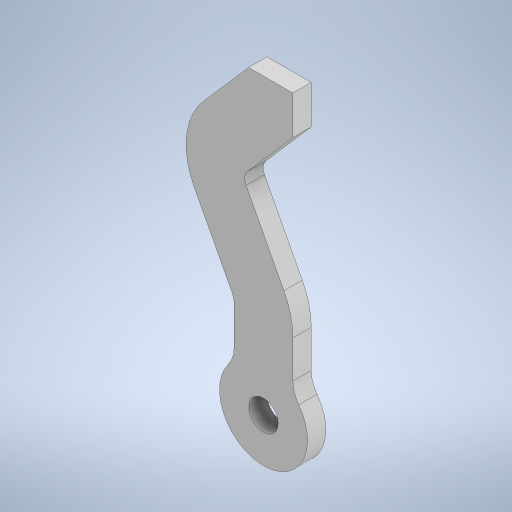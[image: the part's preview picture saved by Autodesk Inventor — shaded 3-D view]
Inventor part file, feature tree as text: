
AUTODESK INVENTOR PART (.ipt)
format: ipt  version: 2023.2 (Build 272271000, 271)  size: 268,288 bytes
history: native  units: mm
features: other x3, sketch x2, extrude x1
ambient origin geometry x8: Origin, YZ Plane, XZ Plane, XY Plane, X Axis, Y Axis, Z Axis, Center Point
bodies: Solid1 (feature_tree)
feature tree (6):
  other  "gripper.ipt"
  extrude  "Extrusion1"  Depth=4.0mm
  other  "Solid1::gripper.ipt"
  other  "TaggingFeature1"
  sketch  "Sketch1"  dims[d0=10.0mm d1=4.0mm]
  sketch  "Sketch2"  dims[d2=10.0mm d3=0.0mm]
